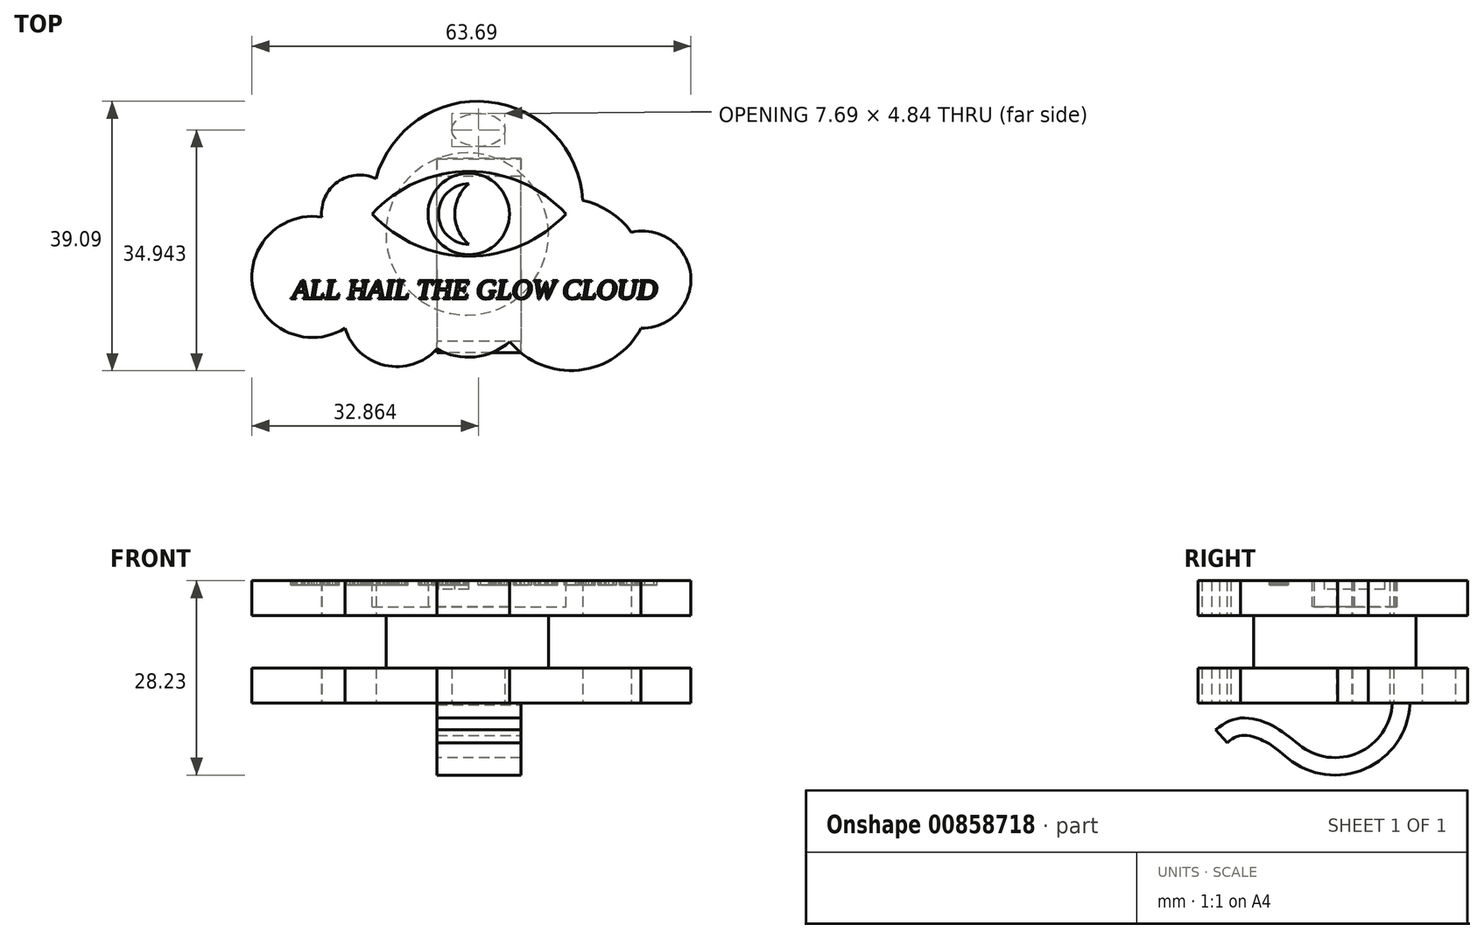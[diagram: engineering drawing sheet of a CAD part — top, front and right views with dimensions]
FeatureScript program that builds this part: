
annotation { "Feature Type Name" : "Feature", "Feature Type Description" : "" }
export const myFeature = defineFeature(function(context is Context, id is Id, definition is map)
    precondition{}
    {
        {
            var Q0;
            Q0=qCreatedBy(makeId("Top.planeOp"),FACE);
            var sketch = newSketch(context, id + "F0", { "sketchPlane" : qUnion([Q0])});
            skArc(sketch, "E0", {"start": v(51.64, -16.97) * mm, "mid": v(37.98, -2.66) * mm, "end": v(21.64, -13.82) * mm});
            skArc(sketch, "E1", {"start": v(21.64, -13.82) * mm, "mid": v(16.07, -14.29) * mm, "end": v(13.77, -19.38) * mm});
            skArc(sketch, "E2", {"start": v(58.69, -21.58) * mm, "mid": v(55.58, -18.64) * mm, "end": v(51.64, -16.97) * mm});
            skArc(sketch, "E3", {"start": v(60.08, -35.51) * mm, "mid": v(67.28, -27.76) * mm, "end": v(58.69, -21.58) * mm});
            skArc(sketch, "E4", {"start": v(41.05, -37.48) * mm, "mid": v(51.1, -41.6) * mm, "end": v(60.08, -35.51) * mm});
            skArc(sketch, "E5", {"start": v(30.49, -38.53) * mm, "mid": v(35.93, -39.68) * mm, "end": v(41.05, -37.48) * mm});
            skArc(sketch, "E6", {"start": v(17.14, -35.51) * mm, "mid": v(22.94, -40.9) * mm, "end": v(30.49, -38.53) * mm});
            skArc(sketch, "E7", {"start": v(13.77, -19.38) * mm, "mid": v(3.82, -29.87) * mm, "end": v(17.14, -35.51) * mm});
            skSolve(sketch);
        }
        {
            var Q0;
            Q0 = qSketchRegion(id + "F0", true);
            extrude(context, id + "F1", {"entities" : qUnion([Q0]), "depth" : 17.78 * mm, "offsetDistance" : 25.4 * mm});
        }
        {
            var Q0;
            Q0=makeQuery(id+"F1.opExtrude","CAP_FACE",FACE,{"disambiguationData":[OSD([sQuery(id+"F0.wireOp",EDGE,"E0"),sQuery(id+"F0.wireOp",EDGE,"E1"),sQuery(id+"F0.wireOp",EDGE,"E2"),sQuery(id+"F0.wireOp",EDGE,"E3"),sQuery(id+"F0.wireOp",EDGE,"E4"),sQuery(id+"F0.wireOp",EDGE,"E5"),sQuery(id+"F0.wireOp",EDGE,"E6"),sQuery(id+"F0.wireOp",EDGE,"E7")])],"isStart":false});
            var sketch = newSketch(context, id + "F2", { "sketchPlane" : qUnion([Q0])});
            skText(sketch, "E8", { "text": "ALL HAIL THE GLOW CLOUD", "fontName": "Tinos-Italic.ttf"});
            const initialGuessF2  = {"E8": [0.0095, -0.03126, 1, 0, 0.00292]};
            skSetInitialGuess(sketch, initialGuessF2);
            skSolve(sketch);
        }
        {
            var Q0;
            Q0 = qSketchRegion(id + "F2", true);
            extrude(context, id + "F3", {"entities" : qUnion([Q0]), "operationType" : NewBodyOperationType.REMOVE, "oppositeDirection" : true, "depth" : 0.64 * mm, "offsetDistance" : 25.4 * mm});
        }
        {
            var Q0;
            {var subQ0=sQuery(id+"F0.wireOp",EDGE,"E2");var subQ1=sQuery(id+"F0.wireOp",EDGE,"E7");var subQ2=sQuery(id+"F0.wireOp",EDGE,"E6");var subQ3=sQuery(id+"F0.wireOp",EDGE,"E5");var subQ4=sQuery(id+"F0.wireOp",EDGE,"E4");var subQ5=sQuery(id+"F0.wireOp",EDGE,"E0");var subQ6=sQuery(id+"F0.wireOp",EDGE,"E3");var subQ7=sQuery(id+"F0.wireOp",EDGE,"E1");Q0=makeQuery(id+"F3.boolean.opBoolean","SPLIT",FACE,{"disambiguationData":[TD([makeQuery(id+"F1.opExtrude","SWEPT_FACE",FACE,{"disambiguationData":[OSD([subQ5])]})])],"derivedFrom":makeQuery(id+"F1.opExtrude","CAP_FACE",FACE,{"disambiguationData":[OSD([subQ5,subQ7,subQ0,subQ6,subQ4,subQ3,subQ2,subQ1])],"isStart":false})});}
            var sketch = newSketch(context, id + "F4", { "sketchPlane" : qUnion([Q0])});
            skArc(sketch, "E9", {"start": v(49.2, -18.91) * mm, "mid": v(35.13, -12.76) * mm, "end": v(21.08, -18.91) * mm});
            skArc(sketch, "E10.MirrorCS", {"start": v(49.2, -18.91) * mm, "mid": v(35.13, -25.07) * mm, "end": v(21.08, -18.91) * mm});
            skSolve(sketch);
        }
        {
            var Q0;
            Q0 = qSketchRegion(id + "F4", true);
            extrude(context, id + "F5", {"entities" : qUnion([Q0]), "operationType" : NewBodyOperationType.REMOVE, "oppositeDirection" : true, "depth" : 3.8 * mm, "offsetDistance" : 25.4 * mm});
        }
        {
            var Q0;
            Q0=makeQuery(id+"F5.boolean.opBoolean","COPY",FACE,{"derivedFrom":makeQuery(id+"F5.opExtrude","CAP_FACE",FACE,{"disambiguationData":[OSD([sQuery(id+"F4.wireOp",EDGE,"E9"),sQuery(id+"F4.wireOp",EDGE,"E10.MirrorCS")])],"isStart":false})});
            var sketch = newSketch(context, id + "F6", { "sketchPlane" : qUnion([Q0])});
            skCircle(sketch, "E11", {"center": v(35.09, -18.94) * mm, "radius": 5.9 * mm});
            skSolve(sketch);
        }
        {
            var Q0;
            Q0 = qSketchRegion(id + "F6", true);
            extrude(context, id + "F7", {"entities" : qUnion([Q0]), "operationType" : NewBodyOperationType.ADD, "depth" : 3.8 * mm, "offsetDistance" : 25.4 * mm});
        }
        {
            var Q0;
            Q0=makeQuery(id+"F7.opExtrude","CAP_FACE",FACE,{"disambiguationData":[OSD([sQuery(id+"F6.wireOp",EDGE,"E11")])],"isStart":false});
            var sketch = newSketch(context, id + "F8", { "sketchPlane" : qUnion([Q0])});
            skPoint(sketch, "E12.first.point", {"position": v(29.18, -18.95) * mm});
            skPoint(sketch, "E12.second.point", {"position": v(40.81, -17.48) * mm});
            skPoint(sketch, "E12.third.point", {"position": v(40.97, -19.47) * mm});
            skArc(sketch, "E13", {"start": v(35.09, -14.56) * mm, "mid": v(30.7, -18.94) * mm, "end": v(35.09, -23.32) * mm});
            skArc(sketch, "E14", {"start": v(35.09, -14.56) * mm, "mid": v(33.07, -18.94) * mm, "end": v(35.09, -23.32) * mm});
            skSolve(sketch);
        }
        {
            var Q0;
            Q0 = qSketchRegion(id + "F8", true);
            extrude(context, id + "F9", {"entities" : qUnion([Q0]), "operationType" : NewBodyOperationType.REMOVE, "oppositeDirection" : true, "depth" : 1.27 * mm, "offsetDistance" : 25.4 * mm});
        }
        {
            var Q0;
            {var subQ0=sQuery(id+"F0.wireOp",EDGE,"E2");var subQ1=sQuery(id+"F0.wireOp",EDGE,"E7");var subQ2=sQuery(id+"F0.wireOp",EDGE,"E6");var subQ3=sQuery(id+"F0.wireOp",EDGE,"E5");var subQ4=sQuery(id+"F0.wireOp",EDGE,"E4");var subQ5=sQuery(id+"F0.wireOp",EDGE,"E0");var subQ6=sQuery(id+"F0.wireOp",EDGE,"E3");var subQ7=sQuery(id+"F0.wireOp",EDGE,"E1");Q0=makeQuery(id+"F3.boolean.opBoolean","SPLIT",FACE,{"disambiguationData":[TD([makeQuery(id+"F1.opExtrude","SWEPT_FACE",FACE,{"disambiguationData":[OSD([subQ5])]})])],"derivedFrom":makeQuery(id+"F1.opExtrude","CAP_FACE",FACE,{"disambiguationData":[OSD([subQ5,subQ7,subQ0,subQ6,subQ4,subQ3,subQ2,subQ1])],"isStart":false})});}
            cPlane(context, id + "F10", {"entities" : qUnion([Q0]), "cplaneType" : CPlaneType.OFFSET, "offset" : 8.9 * mm, "oppositeDirection" : true, "width" : 152.4 * mm, "height" : 152.4 * mm});
        }
        {
            var Q0;
            Q0=qCreatedBy(id+"F10.planeOp",FACE);
            var sketch = newSketch(context, id + "F11", { "sketchPlane" : qUnion([Q0])});
            skCircle(sketch, "E15", {"center": v(34.86, -21.85) * mm, "radius": 11.78 * mm});
            skLineSegment(sketch, "E16.bottom", {"start": v(74.1, 10.25) * mm, "end": v(-11.05, 10.25) * mm});
            skLineSegment(sketch, "E16.top", {"start": v(74.1, -56.34) * mm, "end": v(-11.05, -56.34) * mm});
            skLineSegment(sketch, "E16.left", {"start": v(74.1, 10.25) * mm, "end": v(74.1, -56.34) * mm});
            skLineSegment(sketch, "E16.right", {"start": v(-11.05, 10.25) * mm, "end": v(-11.05, -56.34) * mm});
            skSolve(sketch);
        }
        {
            var Q0;
            Q0 = qSketchRegion(id + "F11", true);
            extrude(context, id + "F12", {"entities" : qUnion([Q0]), "operationType" : NewBodyOperationType.REMOVE, "endBound" : BoundingType.SYMMETRIC, "oppositeDirection" : true, "depth" : 7.62 * mm, "offsetDistance" : 25.4 * mm});
        }
        {
            var Q0;
            Q0=makeQuery(id+"F1.opExtrude","CAP_FACE",FACE,{"disambiguationData":[OSD([sQuery(id+"F0.wireOp",EDGE,"E0"),sQuery(id+"F0.wireOp",EDGE,"E1"),sQuery(id+"F0.wireOp",EDGE,"E2"),sQuery(id+"F0.wireOp",EDGE,"E3"),sQuery(id+"F0.wireOp",EDGE,"E4"),sQuery(id+"F0.wireOp",EDGE,"E5"),sQuery(id+"F0.wireOp",EDGE,"E6"),sQuery(id+"F0.wireOp",EDGE,"E7")])],"isStart":true});
            var sketch = newSketch(context, id + "F13", { "sketchPlane" : qUnion([Q0])});
            skEllipse(sketch, "E17", {"center": v(36.5, 6.73) * mm, "majorRadius": 3.84 * mm, "minorRadius": 2.42 * mm, "majorAxis": v(-1, 0)});
            skSolve(sketch);
        }
        {
            var Q0;
            Q0 = qSketchRegion(id + "F13", true);
            extrude(context, id + "F14", {"entities" : qUnion([Q0]), "operationType" : NewBodyOperationType.REMOVE, "oppositeDirection" : true, "depth" : 12.7 * mm, "offsetDistance" : 25.4 * mm});
        }
        {
            var Q0;
            Q0=qCreatedBy(makeId("Right.planeOp"),FACE);
            cPlane(context, id + "F15", {"entities" : qUnion([Q0]), "cplaneType" : CPlaneType.OFFSET, "offset" : 36.58 * mm, "width" : 152.4 * mm, "height" : 152.4 * mm});
        }
        {
            var Q0;
            Q0=qCreatedBy(id+"F15.planeOp",FACE);
            var sketch = newSketch(context, id + "F16", { "sketchPlane" : qUnion([Q0])});
            skArc(sketch, "E18", {"start": v(-27.02, -6.04) * mm, "mid": v(-18.39, -7.19) * mm, "end": v(-13.46, 0) * mm});
            skFitSpline(sketch, "E19", {"points": [v(-27.02, -6.04) * mm, v(-31.6, -2.92) * mm, v(-36.73, -2.42) * mm, v(-41.22, -6.04) * mm], "startDerivative": vector(-13, 10.6) * mm, "endDerivative": vector(-12.27, -13.4) * mm});
            skArc(sketch, "E20.0", {"start": v(-28.63, -8) * mm, "mid": v(-17.4, -9.53) * mm, "end": v(-10.93, -0.23) * mm});
            skFitSpline(sketch, "E20.1", {"points": [v(-28.63, -8) * mm, v(-29.17, -7.56) * mm, v(-30.2, -6.72) * mm, v(-31.42, -5.86) * mm, v(-32.26, -5.41) * mm, v(-32.73, -5.2) * mm, v(-33.21, -5) * mm, v(-33.82, -4.82) * mm, v(-34.52, -4.7) * mm, v(-35.15, -4.68) * mm, v(-35.6, -4.74) * mm, v(-35.87, -4.8) * mm, v(-36.02, -4.86) * mm, v(-36.25, -4.96) * mm, v(-36.64, -5.17) * mm, v(-37.24, -5.61) * mm, v(-37.9, -6.21) * mm, v(-38.6, -6.93) * mm, v(-39.1, -7.48) * mm, v(-39.35, -7.75) * mm]});
            skLineSegment(sketch, "E21", {"start": v(-39.1, -3.87) * mm, "end": v(-37.42, -5.79) * mm});
            skFitSpline(sketch, "E22", {"points": [v(-10.93, -0.23) * mm, v(-10.92, -0.1) * mm, v(-10.91, 0) * mm], "startDerivative": vector(0.04, 0.3) * mm, "endDerivative": vector(0.01, 0.15) * mm});
            skLineSegment(sketch, "E23", {"start": v(-10.91, 0) * mm, "end": v(-13.46, 0) * mm});
            skSolve(sketch);
        }
        {
            var Q0;
            Q0 = qSketchRegion(id + "F16", true);
            extrude(context, id + "F17", {"entities" : qUnion([Q0]), "operationType" : NewBodyOperationType.ADD, "endBound" : BoundingType.SYMMETRIC, "depth" : 12.2 * mm, "offsetDistance" : 25.4 * mm});
        }
    });
